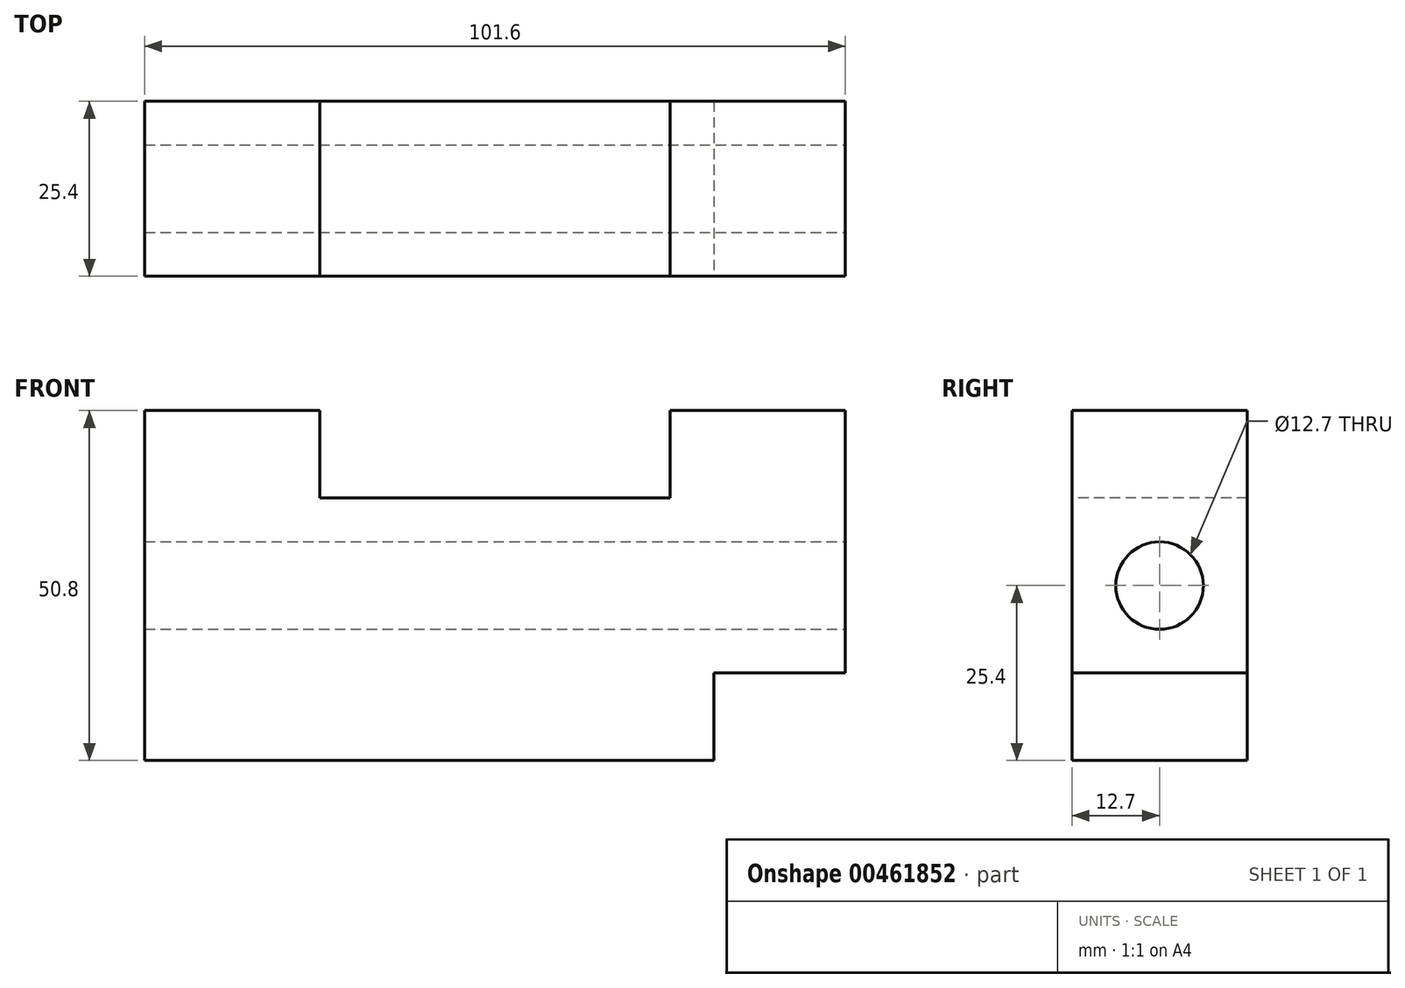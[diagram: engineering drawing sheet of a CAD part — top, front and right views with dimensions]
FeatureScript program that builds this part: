
annotation { "Feature Type Name" : "Feature", "Feature Type Description" : "" }
export const myFeature = defineFeature(function(context is Context, id is Id, definition is map)
    precondition{}
    {
        {
            var Q0;
            Q0=qCreatedBy(makeId("Front.planeOp"),FACE);
            var sketch = newSketch(context, id + "F0", { "sketchPlane" : qUnion([Q0])});
            skLineSegment(sketch, "E0.bottom", {"start": v(-50.8, 25.4) * mm, "end": v(50.8, 25.4) * mm});
            skLineSegment(sketch, "E0.top", {"start": v(-50.8, -25.4) * mm, "end": v(50.8, -25.4) * mm});
            skLineSegment(sketch, "E0.left", {"start": v(-50.8, 25.4) * mm, "end": v(-50.8, -25.4) * mm});
            skLineSegment(sketch, "E0.right", {"start": v(50.8, 25.4) * mm, "end": v(50.8, -25.4) * mm});
            skPoint(sketch, "E0.middle", {"position": v(0, 0) * mm});
            skSolve(sketch);
        }
        {
            var Q0;
            Q0 = qSketchRegion(id + "F0", true);
            extrude(context, id + "F1", {"entities" : qUnion([Q0]), "depth" : 25.4 * mm});
        }
        {
            var Q0;
            Q0=makeQuery(id+"F1.opExtrude","CAP_FACE",FACE,{"disambiguationData":[OSD([sQuery(id+"F0.wireOp",EDGE,"E0.bottom"),sQuery(id+"F0.wireOp",EDGE,"E0.top"),sQuery(id+"F0.wireOp",EDGE,"E0.left"),sQuery(id+"F0.wireOp",EDGE,"E0.right")])],"isStart":false});
            var sketch = newSketch(context, id + "F2", { "sketchPlane" : qUnion([Q0])});
            skLineSegment(sketch, "E1.bottom", {"start": v(-25.4, 25.4) * mm, "end": v(25.4, 25.4) * mm});
            skLineSegment(sketch, "E1.top", {"start": v(-25.4, 12.7) * mm, "end": v(25.4, 12.7) * mm});
            skLineSegment(sketch, "E1.left", {"start": v(-25.4, 25.4) * mm, "end": v(-25.4, 12.7) * mm});
            skLineSegment(sketch, "E1.right", {"start": v(25.4, 25.4) * mm, "end": v(25.4, 12.7) * mm});
            skSolve(sketch);
        }
        {
            var Q0;
            Q0 = qSketchRegion(id + "F2", true);
            extrude(context, id + "F3", {"entities" : qUnion([Q0]), "operationType" : NewBodyOperationType.REMOVE, "endBound" : BoundingType.THROUGH_ALL, "oppositeDirection" : true, "depth" : 25.4 * mm});
        }
        {
            var Q0;
            Q0=makeQuery(id+"F1.opExtrude","CAP_FACE",FACE,{"disambiguationData":[OSD([sQuery(id+"F0.wireOp",EDGE,"E0.bottom"),sQuery(id+"F0.wireOp",EDGE,"E0.top"),sQuery(id+"F0.wireOp",EDGE,"E0.left"),sQuery(id+"F0.wireOp",EDGE,"E0.right")])],"isStart":false});
            var sketch = newSketch(context, id + "F4", { "sketchPlane" : qUnion([Q0])});
            skLineSegment(sketch, "E2.bottom", {"start": v(50.8, -25.4) * mm, "end": v(31.75, -25.4) * mm});
            skLineSegment(sketch, "E2.top", {"start": v(50.8, -12.7) * mm, "end": v(31.75, -12.7) * mm});
            skLineSegment(sketch, "E2.left", {"start": v(50.8, -25.4) * mm, "end": v(50.8, -12.7) * mm});
            skLineSegment(sketch, "E2.right", {"start": v(31.75, -25.4) * mm, "end": v(31.75, -12.7) * mm});
            skSolve(sketch);
        }
        {
            var Q0;
            Q0 = qSketchRegion(id + "F4", true);
            extrude(context, id + "F5", {"entities" : qUnion([Q0]), "operationType" : NewBodyOperationType.REMOVE, "endBound" : BoundingType.THROUGH_ALL, "oppositeDirection" : true, "depth" : 25.4 * mm});
        }
        {
            var Q0;
            Q0=makeQuery(id+"F1.opExtrude","SWEPT_FACE",FACE,{"disambiguationData":[OSD([sQuery(id+"F0.wireOp",EDGE,"E0.right")])]});
            var sketch = newSketch(context, id + "F6", { "sketchPlane" : qUnion([Q0])});
            skCircle(sketch, "E3", {"center": v(-12.7, 0) * mm, "radius": 6.35 * mm});
            skPoint(sketch, "E3.centerSnap0", {"position": v(-12.7, 25.4) * mm});
            skSolve(sketch);
        }
        {
            var Q0;
            Q0 = qSketchRegion(id + "F6", true);
            extrude(context, id + "F7", {"entities" : qUnion([Q0]), "operationType" : NewBodyOperationType.REMOVE, "endBound" : BoundingType.THROUGH_ALL, "oppositeDirection" : true, "depth" : 25.4 * mm});
        }
    });
